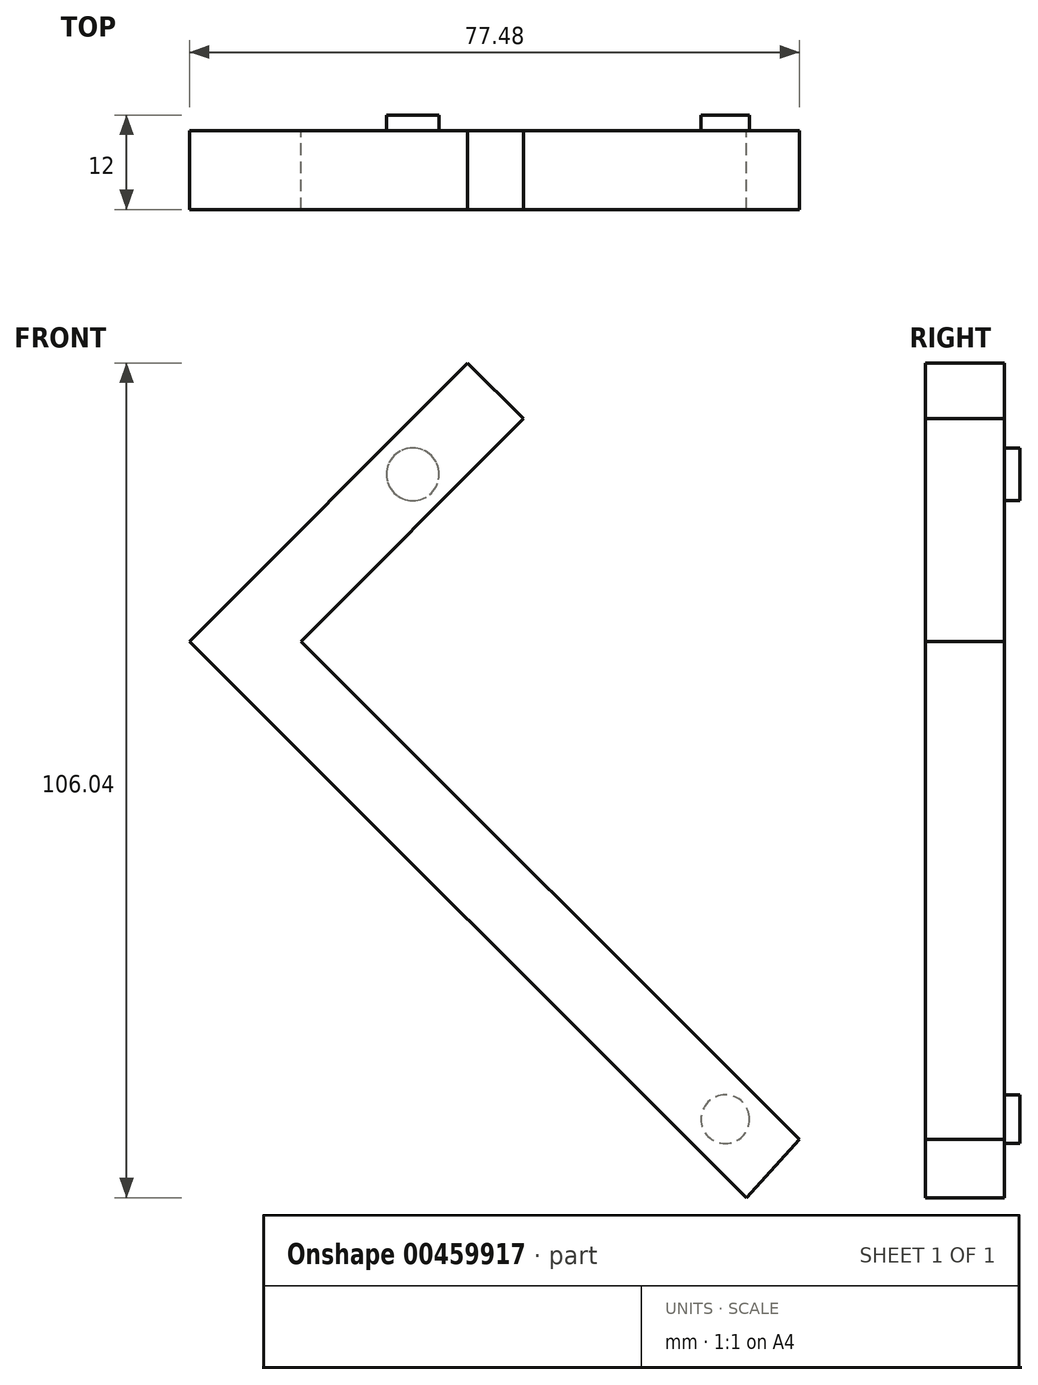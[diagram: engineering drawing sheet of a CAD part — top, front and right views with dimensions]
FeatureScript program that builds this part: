
annotation { "Feature Type Name" : "Feature", "Feature Type Description" : "" }
export const myFeature = defineFeature(function(context is Context, id is Id, definition is map)
    precondition{}
    {
        {
            var Q0;
            Q0=qCreatedBy(makeId("Front.planeOp"),FACE);
            var sketch = newSketch(context, id + "F0", { "sketchPlane" : qUnion([Q0])});
            skLineSegment(sketch, "E0", {"start": v(-61.04, 22.48) * mm, "end": v(9.72, -48.2) * mm});
            skLineSegment(sketch, "E1", {"start": v(-61.04, 22.48) * mm, "end": v(-25.7, 57.85) * mm});
            skLineSegment(sketch, "E2", {"start": v(-25.7, 57.85) * mm, "end": v(-18.62, 50.79) * mm});
            skLineSegment(sketch, "E3", {"start": v(-18.62, 50.79) * mm, "end": v(-46.9, 22.48) * mm});
            skLineSegment(sketch, "E4", {"start": v(-46.9, 22.48) * mm, "end": v(16.44, -40.79) * mm});
            skLineSegment(sketch, "E5", {"start": v(16.44, -40.79) * mm, "end": v(9.72, -48.2) * mm});
            skSolve(sketch);
        }
        {
            var Q0;
            Q0=makeQuery(id+"F0.imprint","IMPRINT",FACE,{"disambiguationData":[TD([[makeQuery(id+"F0.imprint","IMPRINT",EDGE,{"derivedFrom":sQuery(id+"F0.wireOp",EDGE,"E0")}),1.0]])]});
            extrude(context, id + "F1", {"entities" : qUnion([Q0]), "depth" : 10 * mm});
        }
        {
            var Q0;
            Q0=makeQuery(id+"F1.opExtrude","CAP_FACE",FACE,{"disambiguationData":[OSD([sQuery(id+"F0.wireOp",EDGE,"E0"),sQuery(id+"F0.wireOp",EDGE,"E1"),sQuery(id+"F0.wireOp",EDGE,"E2"),sQuery(id+"F0.wireOp",EDGE,"E3"),sQuery(id+"F0.wireOp",EDGE,"E4"),sQuery(id+"F0.wireOp",EDGE,"E5")])],"isStart":true});
            var sketch = newSketch(context, id + "F2", { "sketchPlane" : qUnion([Q0])});
            skCircle(sketch, "E6", {"center": v(-7.01, -38.23) * mm, "radius": 3.08 * mm});
            skCircle(sketch, "E7", {"center": v(32.67, 43.7) * mm, "radius": 3.35 * mm});
            skSolve(sketch);
        }
        {
            var Q0;
            Q0=makeQuery(id+"F2.imprint","IMPRINT",FACE,{"disambiguationData":[TD([[makeQuery(id+"F2.imprint","IMPRINT",EDGE,{"derivedFrom":sQuery(id+"F2.wireOp",EDGE,"E6")}),1.0]])]});
            var Q1;
            Q1=makeQuery(id+"F2.imprint","IMPRINT",FACE,{"disambiguationData":[TD([[makeQuery(id+"F2.imprint","IMPRINT",EDGE,{"derivedFrom":sQuery(id+"F2.wireOp",EDGE,"E7")}),1.0]])]});
            extrude(context, id + "F3", {"entities" : qUnion([Q0, Q1]), "operationType" : NewBodyOperationType.ADD, "depth" : 2 * mm});
        }
    });
